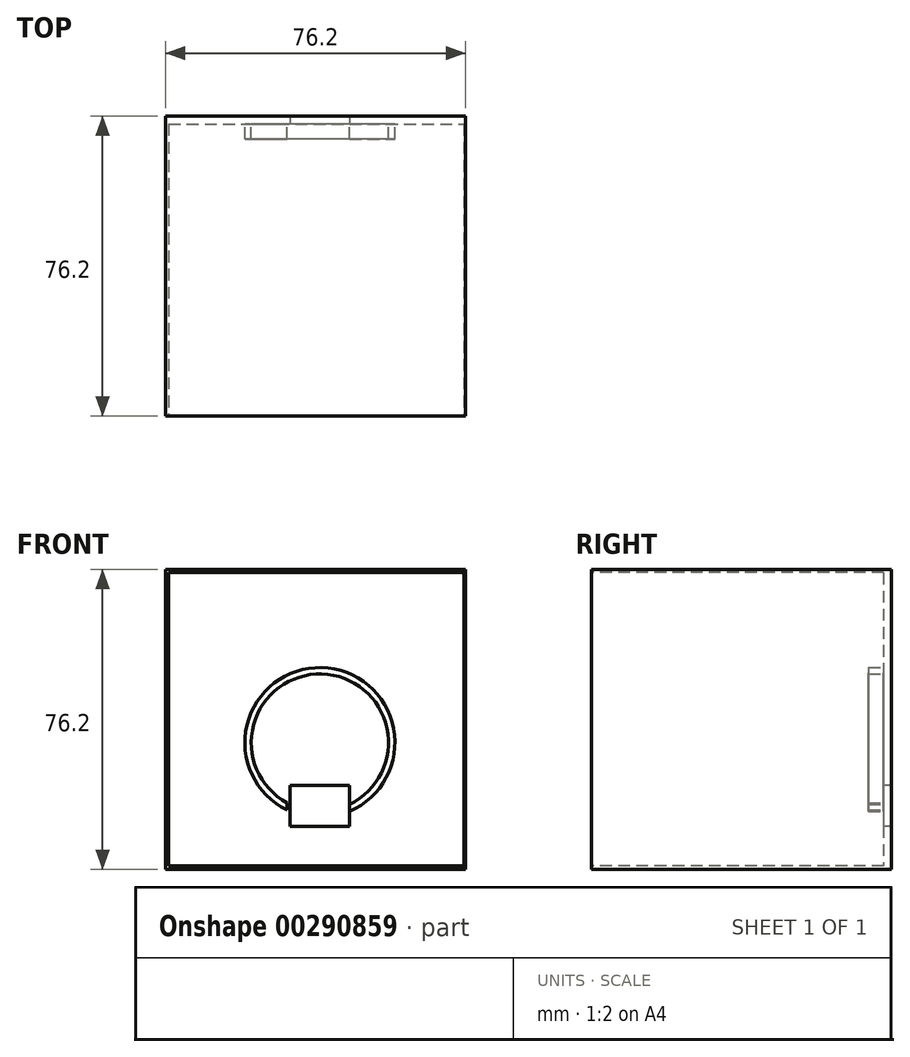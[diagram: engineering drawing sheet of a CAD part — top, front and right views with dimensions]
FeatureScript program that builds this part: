
annotation { "Feature Type Name" : "Feature", "Feature Type Description" : "" }
export const myFeature = defineFeature(function(context is Context, id is Id, definition is map)
    precondition{}
    {
        {
            var Q0;
            Q0=qCreatedBy(makeId("Front.planeOp"),FACE);
            var sketch = newSketch(context, id + "F0", { "sketchPlane" : qUnion([Q0])});
            skLineSegment(sketch, "E0.bottom", {"start": v(0, 0) * mm, "end": v(-76.2, 0) * mm});
            skLineSegment(sketch, "E0.top", {"start": v(0, 76.2) * mm, "end": v(-76.2, 76.2) * mm});
            skLineSegment(sketch, "E0.left", {"start": v(0, 0) * mm, "end": v(0, 76.2) * mm});
            skLineSegment(sketch, "E0.right", {"start": v(-76.2, 0) * mm, "end": v(-76.2, 76.2) * mm});
            skSolve(sketch);
        }
        {
            var Q0;
            Q0 = qSketchRegion(id + "F0", true);
            extrude(context, id + "F1", {"entities" : qUnion([Q0]), "depth" : 76.2 * mm});
        }
        {
            var Q0;
            Q0=makeQuery(id+"F1.opExtrude","CAP_FACE",FACE,{"disambiguationData":[OSD([sQuery(id+"F0.wireOp",EDGE,"E0.bottom"),sQuery(id+"F0.wireOp",EDGE,"E0.top"),sQuery(id+"F0.wireOp",EDGE,"E0.left"),sQuery(id+"F0.wireOp",EDGE,"E0.right")])],"isStart":false});
            var sketch = newSketch(context, id + "F2", { "sketchPlane" : qUnion([Q0])});
            skLineSegment(sketch, "E1.bottom", {"start": v(-75.4, 75.4) * mm, "end": v(-0.4, 75.4) * mm});
            skLineSegment(sketch, "E1.top", {"start": v(-75.4, 0.87) * mm, "end": v(-0.4, 0.87) * mm});
            skLineSegment(sketch, "E1.left", {"start": v(-75.4, 75.4) * mm, "end": v(-75.4, 0.87) * mm});
            skLineSegment(sketch, "E1.right", {"start": v(-0.4, 75.4) * mm, "end": v(-0.4, 0.87) * mm});
            skSolve(sketch);
        }
        {
            var Q0;
            Q0 = qSketchRegion(id + "F2", true);
            extrude(context, id + "F3", {"entities" : qUnion([Q0]), "operationType" : NewBodyOperationType.REMOVE, "oppositeDirection" : true, "depth" : 74.22 * mm});
        }
        {
            var Q0;
            Q0=makeQuery(id+"F3.boolean.opBoolean","COPY",FACE,{"derivedFrom":makeQuery(id+"F3.opExtrude","CAP_FACE",FACE,{"disambiguationData":[OSD([sQuery(id+"F2.wireOp",EDGE,"E1.bottom"),sQuery(id+"F2.wireOp",EDGE,"E1.top"),sQuery(id+"F2.wireOp",EDGE,"E1.left"),sQuery(id+"F2.wireOp",EDGE,"E1.right")])],"isStart":false})});
            var sketch = newSketch(context, id + "F4", { "sketchPlane" : qUnion([Q0])});
            skLineSegment(sketch, "E2.bottom", {"start": v(-29.47, 21.33) * mm, "end": v(-44.52, 21.33) * mm});
            skLineSegment(sketch, "E2.top", {"start": v(-29.47, 10.91) * mm, "end": v(-44.52, 10.91) * mm});
            skLineSegment(sketch, "E2.left", {"start": v(-29.47, 21.33) * mm, "end": v(-29.47, 10.91) * mm});
            skLineSegment(sketch, "E2.right", {"start": v(-44.52, 21.33) * mm, "end": v(-44.52, 10.91) * mm});
            skSolve(sketch);
        }
        {
            var Q0;
            Q0 = qSketchRegion(id + "F4", true);
            extrude(context, id + "F5", {"entities" : qUnion([Q0]), "operationType" : NewBodyOperationType.REMOVE, "oppositeDirection" : true, "depth" : 23.8 * mm});
        }
        {
            var Q0;
            Q0=makeQuery(id+"F3.boolean.opBoolean","COPY",FACE,{"derivedFrom":makeQuery(id+"F3.opExtrude","CAP_FACE",FACE,{"disambiguationData":[OSD([sQuery(id+"F2.wireOp",EDGE,"E1.bottom"),sQuery(id+"F2.wireOp",EDGE,"E1.top"),sQuery(id+"F2.wireOp",EDGE,"E1.left"),sQuery(id+"F2.wireOp",EDGE,"E1.right")])],"isStart":false})});
            var sketch = newSketch(context, id + "F6", { "sketchPlane" : qUnion([Q0])});
            skArc(sketch, "E3", {"start": v(-29.47, 14.72) * mm, "mid": v(-36.54, 51.27) * mm, "end": v(-45.35, 15.1) * mm});
            skPoint(sketch, "E3.centerSnap0", {"position": v(-37, 21.33) * mm});
            skArc(sketch, "E4", {"start": v(-29.47, 16.5) * mm, "mid": v(-36.53, 49.65) * mm, "end": v(-45.35, 16.92) * mm});
            skLineSegment(sketch, "E5", {"start": v(-45.35, 15.1) * mm, "end": v(-45.35, 16.92) * mm});
            skLineSegment(sketch, "E6", {"start": v(-29.47, 16.5) * mm, "end": v(-29.47, 14.72) * mm});
            skPoint(sketch, "E6.startSnap0", {"position": v(-29.47, 16.12) * mm});
            skSolve(sketch);
        }
        {
            var Q0;
            Q0 = qSketchRegion(id + "F6", true);
            extrude(context, id + "F7", {"entities" : qUnion([Q0]), "operationType" : NewBodyOperationType.ADD, "depth" : 3.8 * mm});
        }
    });
